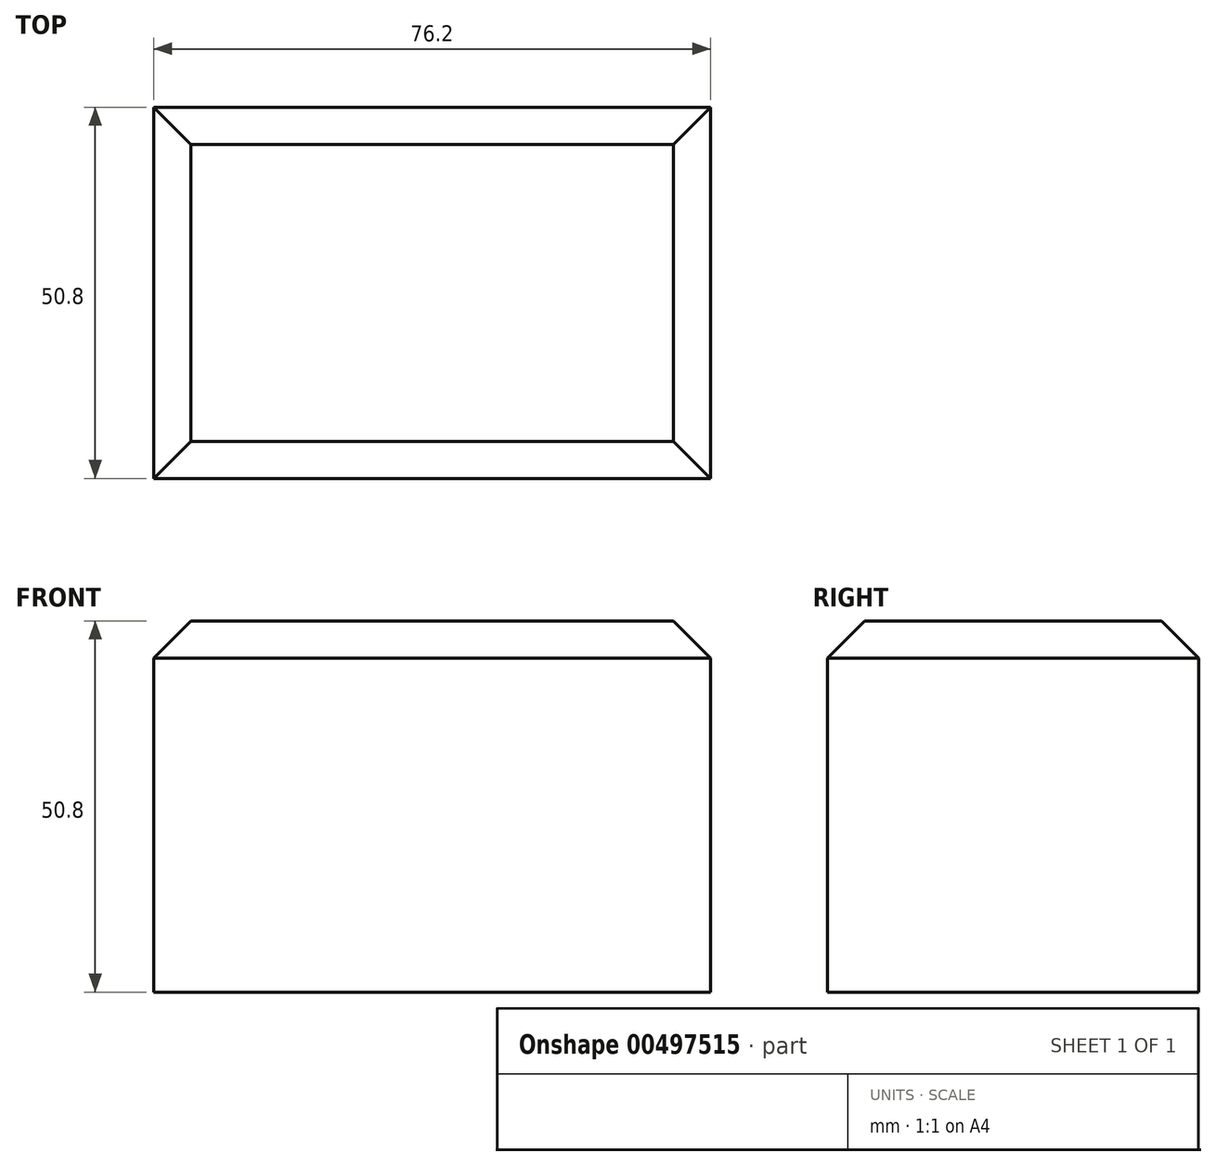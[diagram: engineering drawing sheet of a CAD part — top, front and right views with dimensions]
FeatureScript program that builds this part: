
annotation { "Feature Type Name" : "Feature", "Feature Type Description" : "" }
export const myFeature = defineFeature(function(context is Context, id is Id, definition is map)
    precondition{}
    {
        {
            var Q0;
            Q0=qCreatedBy(makeId("Top.planeOp"),FACE);
            var sketch = newSketch(context, id + "F0", { "sketchPlane" : qUnion([Q0])});
            skLineSegment(sketch, "E0.bottom", {"start": v(-18.87, 21.7) * mm, "end": v(57.33, 21.7) * mm});
            skLineSegment(sketch, "E0.top", {"start": v(-18.87, -29.1) * mm, "end": v(57.33, -29.1) * mm});
            skLineSegment(sketch, "E0.left", {"start": v(-18.87, 21.7) * mm, "end": v(-18.87, -29.1) * mm});
            skLineSegment(sketch, "E0.right", {"start": v(57.33, 21.7) * mm, "end": v(57.33, -29.1) * mm});
            skSolve(sketch);
        }
        {
            var Q0;
            Q0 = qSketchRegion(id + "F0", true);
            var Q1;
            Q1=makeQuery(id+"F0.imprint","IMPRINT",FACE,{"disambiguationData":[TD([[makeQuery(id+"F0.imprint","IMPRINT",EDGE,{"derivedFrom":sQuery(id+"F0.wireOp",EDGE,"E0.bottom")}),-1.0]])]});
            extrude(context, id + "F1", {"entities" : qUnion([Q0, Q1]), "depth" : 50.8 * mm});
        }
        {
            var Q0;
            Q0=makeQuery(id+"F1.opExtrude","CAP_EDGE",EDGE,{"disambiguationData":[OSD([sQuery(id+"F0.wireOp",EDGE,"E0.top")])],"isStart":false});
            var Q1;
            Q1=makeQuery(id+"F1.opExtrude","CAP_EDGE",EDGE,{"disambiguationData":[OSD([sQuery(id+"F0.wireOp",EDGE,"E0.right")])],"isStart":false});
            var Q2;
            Q2=makeQuery(id+"F1.opExtrude","CAP_EDGE",EDGE,{"disambiguationData":[OSD([sQuery(id+"F0.wireOp",EDGE,"E0.bottom")])],"isStart":false});
            var Q3;
            Q3=makeQuery(id+"F1.opExtrude","CAP_FACE",FACE,{"disambiguationData":[OSD([sQuery(id+"F0.wireOp",EDGE,"E0.bottom"),sQuery(id+"F0.wireOp",EDGE,"E0.top"),sQuery(id+"F0.wireOp",EDGE,"E0.left"),sQuery(id+"F0.wireOp",EDGE,"E0.right")])],"isStart":false});
            chamfer(context, id + "F2", {"entities" : qUnion([Q0, Q1, Q2, Q3]), "width" : 5.08 * mm, "tangentPropagation" : true});
        }
    });
